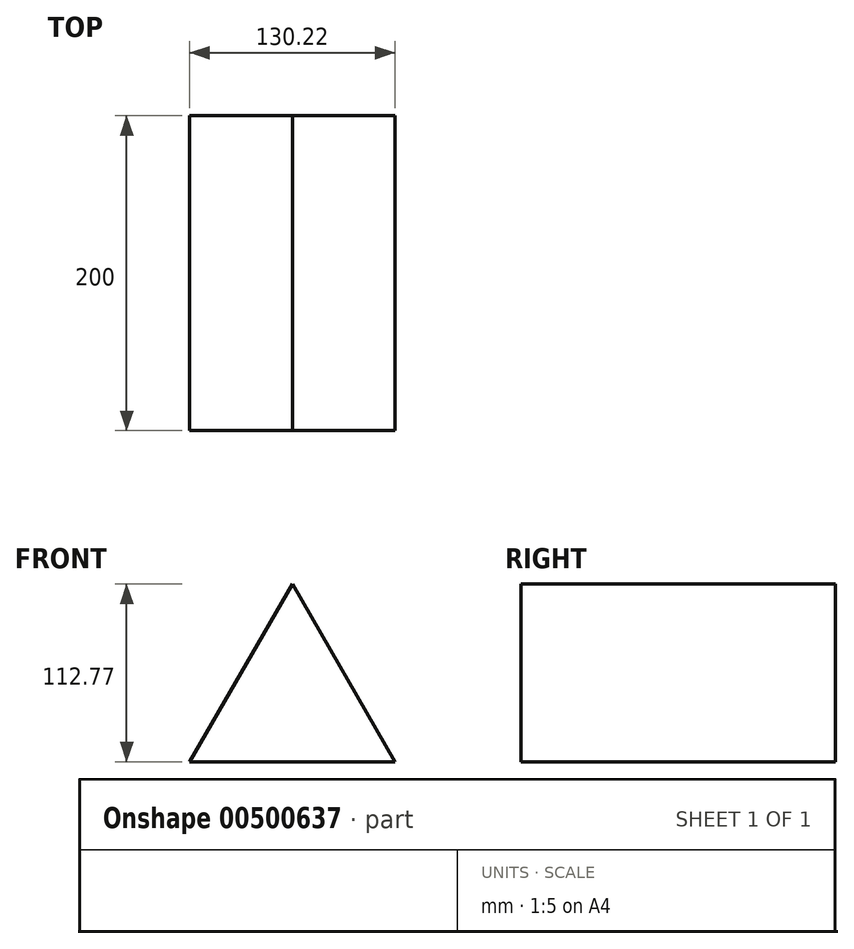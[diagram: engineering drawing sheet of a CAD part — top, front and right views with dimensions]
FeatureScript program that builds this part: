
annotation { "Feature Type Name" : "Feature", "Feature Type Description" : "" }
export const myFeature = defineFeature(function(context is Context, id is Id, definition is map)
    precondition{}
    {
        {
            var Q0;
            Q0=qCreatedBy(makeId("Front.planeOp"),FACE);
            var sketch = newSketch(context, id + "F0", { "sketchPlane" : qUnion([Q0])});
            skCircle(sketch, "E0.cCircle", {"center": v(0, 0) * mm, "radius": 75.18 * mm, "construction": true});
            skLineSegment(sketch, "E0.0", {"start": v(0, 75.18) * mm, "end": v(65.1, -37.59) * mm});
            skLineSegment(sketch, "E0.1", {"start": v(65.1, -37.59) * mm, "end": v(-65.1, -37.59) * mm});
            skLineSegment(sketch, "E0.2", {"start": v(-65.1, -37.59) * mm, "end": v(0, 75.18) * mm});
            skSolve(sketch);
        }
        {
            var Q0;
            Q0 = qSketchRegion(id + "F0", true);
            extrude(context, id + "F1", {"entities" : qUnion([Q0]), "depth" : 200 * mm});
        }
    });
